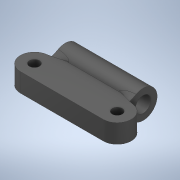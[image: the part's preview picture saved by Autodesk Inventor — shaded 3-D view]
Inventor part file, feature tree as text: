
AUTODESK INVENTOR PART (.ipt)
format: ipt  version: 2020 (Build 240168000, 168)  size: 239,616 bytes
history: native  units: in
note: dims shown in document units (in); Inventor stores cm internally (conversion verified against a paired STEP export)
features: extrude x1, sketch x1
ambient origin geometry x8: Origin, YZ Plane, XZ Plane, XY Plane, X Axis, Y Axis, Z Axis, Center Point
bodies: Solid2 (feature_tree), Solid1 (feature_tree)
feature tree (2):
  extrude  "remove brass inserts"  Depth=0.3937in
  sketch  "Sketch1"  dims[d0=0.126in d1=0.126in d2=0.3937in d3=0.0in d4=0.0197in d5=1.9685in]
